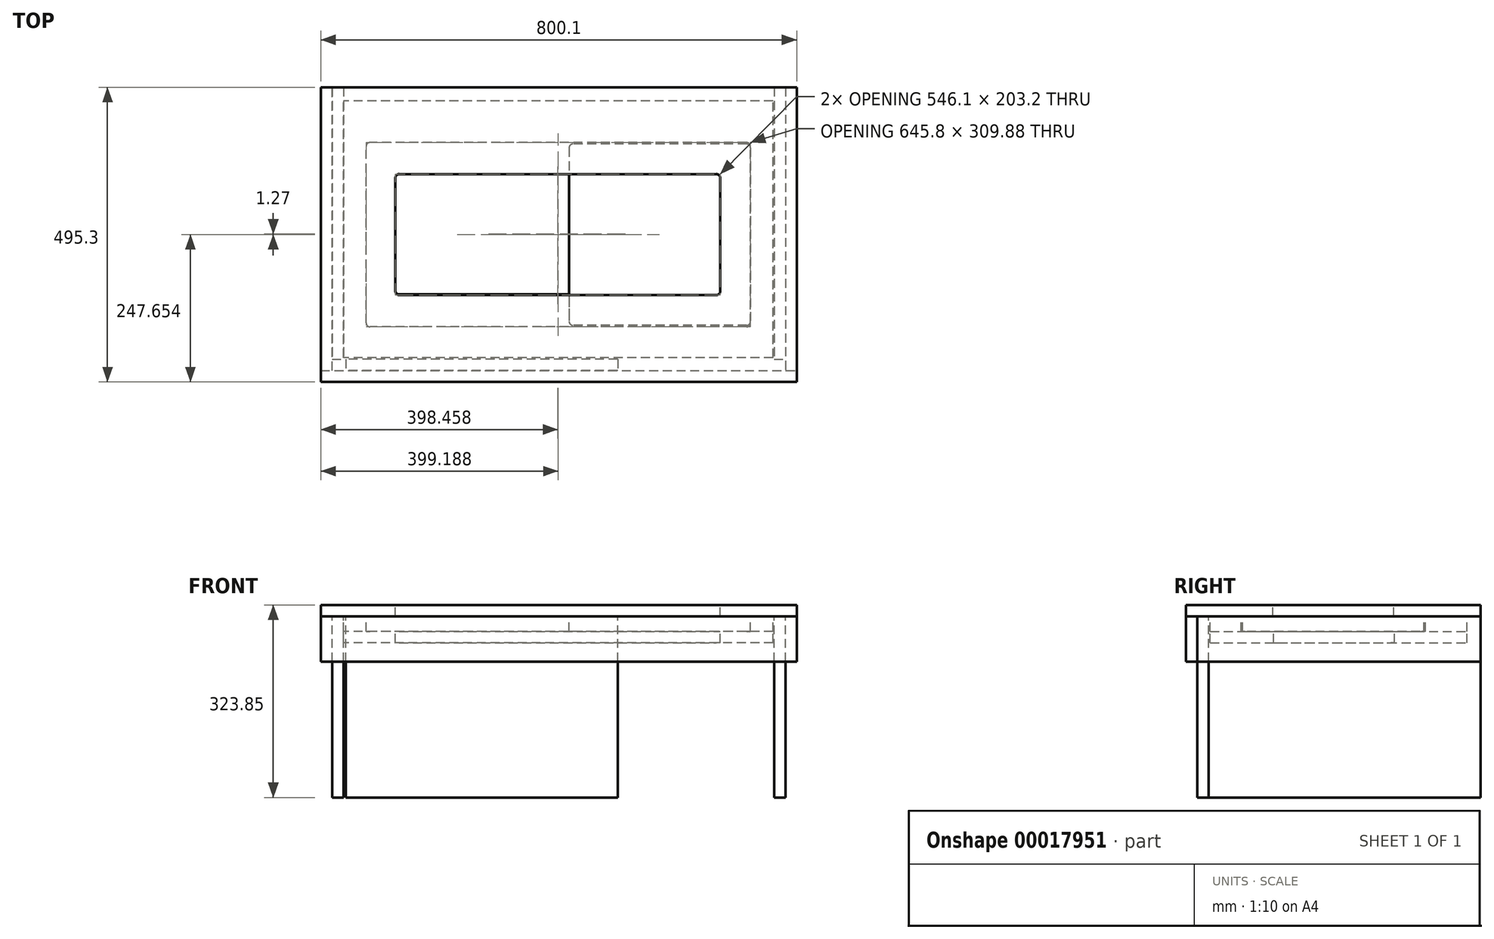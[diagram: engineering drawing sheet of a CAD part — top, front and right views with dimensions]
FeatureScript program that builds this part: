
annotation { "Feature Type Name" : "Feature", "Feature Type Description" : "" }
export const myFeature = defineFeature(function(context is Context, id is Id, definition is map)
    precondition{}
    {
        {
            var Q0;
            Q0=qCreatedBy(makeId("Top.planeOp"),FACE);
            var sketch = newSketch(context, id + "F0", { "sketchPlane" : qUnion([Q0])});
            skLineSegment(sketch, "E0.bottom", {"start": v(-395.07, 146.58) * mm, "end": v(405.03, 146.58) * mm});
            skLineSegment(sketch, "E0.top", {"start": v(-395.07, -348.72) * mm, "end": v(405.03, -348.72) * mm});
            skLineSegment(sketch, "E0.left", {"start": v(-395.07, 146.58) * mm, "end": v(-395.07, -348.72) * mm});
            skLineSegment(sketch, "E0.right", {"start": v(405.03, 146.58) * mm, "end": v(405.03, -348.72) * mm});
            skSolve(sketch);
        }
        {
            var Q0;
            Q0 = qSketchRegion(id + "F0", true);
            extrude(context, id + "F1", {"entities" : qUnion([Q0]), "depth" : 19.05 * mm, "offsetDistance" : 25.4 * mm});
        }
        {
            var Q0;
            Q0=makeQuery(id+"F1.opExtrude","CAP_FACE",FACE,{"disambiguationData":[OSD([sQuery(id+"F0.wireOp",EDGE,"E0.bottom"),sQuery(id+"F0.wireOp",EDGE,"E0.top"),sQuery(id+"F0.wireOp",EDGE,"E0.left"),sQuery(id+"F0.wireOp",EDGE,"E0.right")])],"isStart":false});
            var sketch = newSketch(context, id + "F2", { "sketchPlane" : qUnion([Q0])});
            skLineSegment(sketch, "E1.bottom", {"start": v(-269.66, 0.53) * mm, "end": v(276.44, 0.53) * mm});
            skLineSegment(sketch, "E1.top", {"start": v(-269.66, -202.67) * mm, "end": v(276.44, -202.67) * mm});
            skLineSegment(sketch, "E1.left", {"start": v(-269.66, 0.53) * mm, "end": v(-269.66, -202.67) * mm});
            skLineSegment(sketch, "E1.right", {"start": v(276.44, 0.53) * mm, "end": v(276.44, -202.67) * mm});
            skSolve(sketch);
        }
        {
            var Q0;
            Q0 = qSketchRegion(id + "F2", true);
            extrude(context, id + "F3", {"entities" : qUnion([Q0]), "operationType" : NewBodyOperationType.REMOVE, "oppositeDirection" : true, "depth" : 25.4 * mm, "offsetDistance" : 25.4 * mm});
        }
        {
            var Q0;
            Q0=makeQuery(id+"F3.boolean.opBoolean","COPY",EDGE,{"derivedFrom":makeQuery(id+"F3.opExtrude","SWEPT_EDGE",EDGE,{"disambiguationData":[OSD([sQuery(id+"F2.wireOp",EDGE,"E1.bottom"),sQuery(id+"F2.wireOp",EDGE,"E1.left")])]})});
            var Q1;
            Q1=makeQuery(id+"F3.boolean.opBoolean","COPY",EDGE,{"derivedFrom":makeQuery(id+"F3.opExtrude","SWEPT_EDGE",EDGE,{"disambiguationData":[OSD([sQuery(id+"F2.wireOp",EDGE,"E1.bottom"),sQuery(id+"F2.wireOp",EDGE,"E1.right")])]})});
            var Q2;
            Q2=makeQuery(id+"F3.boolean.opBoolean","COPY",EDGE,{"derivedFrom":makeQuery(id+"F3.opExtrude","SWEPT_EDGE",EDGE,{"disambiguationData":[OSD([sQuery(id+"F2.wireOp",EDGE,"E1.top"),sQuery(id+"F2.wireOp",EDGE,"E1.right")])]})});
            var Q3;
            Q3=makeQuery(id+"F3.boolean.opBoolean","COPY",EDGE,{"derivedFrom":makeQuery(id+"F3.opExtrude","SWEPT_EDGE",EDGE,{"disambiguationData":[OSD([sQuery(id+"F2.wireOp",EDGE,"E1.top"),sQuery(id+"F2.wireOp",EDGE,"E1.left")])]})});
            fillet(context, id + "F4", {"entities" : qUnion([Q0, Q1, Q2, Q3]), "radius" : 6.35 * mm, "tangentPropagation" : true, "allowEdgeOverflow" : false});
        }
        {
            var Q0;
            Q0=makeQuery(id+"F1.opExtrude","CAP_FACE",FACE,{"disambiguationData":[OSD([sQuery(id+"F0.wireOp",EDGE,"E0.bottom"),sQuery(id+"F0.wireOp",EDGE,"E0.top"),sQuery(id+"F0.wireOp",EDGE,"E0.left"),sQuery(id+"F0.wireOp",EDGE,"E0.right")])],"isStart":true});
            var sketch = newSketch(context, id + "F5", { "sketchPlane" : qUnion([Q0])});
            skLineSegment(sketch, "E2.bottom", {"start": v(-395.07, 348.72) * mm, "end": v(405.03, 348.72) * mm});
            skLineSegment(sketch, "E2.top", {"start": v(-395.07, 329.67) * mm, "end": v(405.03, 329.67) * mm});
            skLineSegment(sketch, "E2.left", {"start": v(-395.07, 348.72) * mm, "end": v(-395.07, 329.67) * mm});
            skLineSegment(sketch, "E2.right", {"start": v(405.03, 348.72) * mm, "end": v(405.03, 329.67) * mm});
            skSolve(sketch);
        }
        {
            var Q0;
            Q0 = qSketchRegion(id + "F5", true);
            extrude(context, id + "F6", {"entities" : qUnion([Q0]), "depth" : 76.2 * mm, "offsetDistance" : 25.4 * mm});
        }
        {
            var Q0;
            Q0=makeQuery(id+"F1.opExtrude","CAP_FACE",FACE,{"disambiguationData":[OSD([sQuery(id+"F0.wireOp",EDGE,"E0.bottom"),sQuery(id+"F0.wireOp",EDGE,"E0.top"),sQuery(id+"F0.wireOp",EDGE,"E0.left"),sQuery(id+"F0.wireOp",EDGE,"E0.right")])],"isStart":true});
            var sketch = newSketch(context, id + "F7", { "sketchPlane" : qUnion([Q0])});
            skLineSegment(sketch, "E3.bottom", {"start": v(-395.07, 329.67) * mm, "end": v(-376.02, 329.67) * mm});
            skLineSegment(sketch, "E3.top", {"start": v(-395.07, -146.58) * mm, "end": v(-376.02, -146.58) * mm});
            skLineSegment(sketch, "E3.left", {"start": v(-395.07, 329.67) * mm, "end": v(-395.07, -146.58) * mm});
            skLineSegment(sketch, "E3.right", {"start": v(-376.02, 329.67) * mm, "end": v(-376.02, -146.58) * mm});
            skSolve(sketch);
        }
        {
            var Q0;
            Q0 = qSketchRegion(id + "F7", true);
            extrude(context, id + "F8", {"entities" : qUnion([Q0]), "depth" : 76.2 * mm, "offsetDistance" : 25.4 * mm});
        }
        {
            var Q0;
            Q0=makeQuery(id+"F8.opExtrude","SWEPT_BODY",BODY,{"disambiguationData":[OSD([sQuery(id+"F7.wireOp",EDGE,"E3.bottom"),sQuery(id+"F7.wireOp",EDGE,"E3.top"),sQuery(id+"F7.wireOp",EDGE,"E3.left"),sQuery(id+"F7.wireOp",EDGE,"E3.right")])]});
            transform(context, id + "F9", {"entities" : qUnion([Q0]), "transformType" : TransformType.TRANSLATION_3D, "dx" : 781.05 * mm, "dy" : 0 * mm, "dz" : 0 * mm, "makeCopy" : true});
        }
        {
            var Q0;
            Q0=makeQuery(id+"F1.opExtrude","CAP_FACE",FACE,{"disambiguationData":[OSD([sQuery(id+"F0.wireOp",EDGE,"E0.bottom"),sQuery(id+"F0.wireOp",EDGE,"E0.top"),sQuery(id+"F0.wireOp",EDGE,"E0.left"),sQuery(id+"F0.wireOp",EDGE,"E0.right")])],"isStart":true});
            var sketch = newSketch(context, id + "F10", { "sketchPlane" : qUnion([Q0])});
            skLineSegment(sketch, "E4.bottom", {"start": v(327.24, -51.33) * mm, "end": v(22.44, -51.33) * mm});
            skLineSegment(sketch, "E4.top", {"start": v(327.24, 253.47) * mm, "end": v(22.44, 253.47) * mm});
            skLineSegment(sketch, "E4.left", {"start": v(327.24, -51.33) * mm, "end": v(327.24, 253.47) * mm});
            skLineSegment(sketch, "E4.right", {"start": v(22.44, -51.33) * mm, "end": v(22.44, 253.47) * mm});
            skSolve(sketch);
        }
        {
            var Q0;
            Q0 = qSketchRegion(id + "F10", true);
            extrude(context, id + "F11", {"entities" : qUnion([Q0]), "depth" : 25.4 * mm, "offsetDistance" : 25.4 * mm});
        }
        {
            var Q0;
            Q0=makeQuery(id+"F11.opExtrude","SWEPT_EDGE",EDGE,{"disambiguationData":[OSD([sQuery(id+"F10.wireOp",EDGE,"E4.bottom"),sQuery(id+"F10.wireOp",EDGE,"E4.left")])]});
            var Q1;
            Q1=makeQuery(id+"F11.opExtrude","SWEPT_EDGE",EDGE,{"disambiguationData":[OSD([sQuery(id+"F10.wireOp",EDGE,"E4.bottom"),sQuery(id+"F10.wireOp",EDGE,"E4.right")])]});
            var Q2;
            Q2=makeQuery(id+"F11.opExtrude","SWEPT_EDGE",EDGE,{"disambiguationData":[OSD([sQuery(id+"F10.wireOp",EDGE,"E4.top"),sQuery(id+"F10.wireOp",EDGE,"E4.left")])]});
            var Q3;
            Q3=makeQuery(id+"F11.opExtrude","SWEPT_EDGE",EDGE,{"disambiguationData":[OSD([sQuery(id+"F10.wireOp",EDGE,"E4.top"),sQuery(id+"F10.wireOp",EDGE,"E4.right")])]});
            fillet(context, id + "F12", {"entities" : qUnion([Q0, Q1, Q2, Q3]), "radius" : 6.35 * mm, "tangentPropagation" : true, "allowEdgeOverflow" : false});
        }
        {
            var Q0;
            Q0=makeQuery(id+"F1.opExtrude","CAP_FACE",FACE,{"disambiguationData":[OSD([sQuery(id+"F0.wireOp",EDGE,"E0.bottom"),sQuery(id+"F0.wireOp",EDGE,"E0.top"),sQuery(id+"F0.wireOp",EDGE,"E0.left"),sQuery(id+"F0.wireOp",EDGE,"E0.right")])],"isStart":true});
            var sketch = newSketch(context, id + "F13", { "sketchPlane" : qUnion([Q0])});
            skLineSegment(sketch, "E5.bottom", {"start": v(-376.02, -146.58) * mm, "end": v(-356.97, -146.58) * mm});
            skLineSegment(sketch, "E5.top", {"start": v(-376.02, 310.62) * mm, "end": v(-356.97, 310.62) * mm});
            skLineSegment(sketch, "E5.left", {"start": v(-376.02, -146.58) * mm, "end": v(-376.02, 310.62) * mm});
            skLineSegment(sketch, "E5.right", {"start": v(-356.97, -146.58) * mm, "end": v(-356.97, 310.62) * mm});
            skSolve(sketch);
        }
        {
            var Q0;
            Q0 = qSketchRegion(id + "F13", true);
            extrude(context, id + "F14", {"entities" : qUnion([Q0]), "depth" : 304.8 * mm, "offsetDistance" : 25.4 * mm});
        }
        {
            var Q0;
            Q0=makeQuery(id+"F14.opExtrude","SWEPT_BODY",BODY,{"disambiguationData":[OSD([sQuery(id+"F13.wireOp",EDGE,"E5.bottom"),sQuery(id+"F13.wireOp",EDGE,"E5.top"),sQuery(id+"F13.wireOp",EDGE,"E5.left"),sQuery(id+"F13.wireOp",EDGE,"E5.right")])]});
            transform(context, id + "F15", {"entities" : qUnion([Q0]), "transformType" : TransformType.TRANSLATION_3D, "dx" : 742.95 * mm, "dy" : 0 * mm, "dz" : 0 * mm, "makeCopy" : true});
        }
        {
            var Q0;
            Q0=makeQuery(id+"F14.opExtrude","SWEPT_BODY",BODY,{"disambiguationData":[OSD([sQuery(id+"F13.wireOp",EDGE,"E5.bottom"),sQuery(id+"F13.wireOp",EDGE,"E5.top"),sQuery(id+"F13.wireOp",EDGE,"E5.left"),sQuery(id+"F13.wireOp",EDGE,"E5.right")])]});
            var Q1;
            Q1=makeQuery(id+"F14.opExtrude","SWEPT_EDGE",EDGE,{"disambiguationData":[OSD([sQuery(id+"F13.wireOp",EDGE,"E5.top"),sQuery(id+"F13.wireOp",EDGE,"E5.right")])]});
            transform(context, id + "F16", {"entities" : qUnion([Q0]), "transformType" : TransformType.ROTATION, "transformAxis" : qUnion([Q1]), "angle" : 90 * degree, "oppositeDirection" : true, "makeCopy" : true});
        }
        {
            var Q0;
            Q0=makeQuery(id+"F16.opPattern","COPY",BODY,{"derivedFrom":makeQuery(id+"F14.opExtrude","SWEPT_BODY",BODY,{"disambiguationData":[OSD([sQuery(id+"F13.wireOp",EDGE,"E5.bottom"),sQuery(id+"F13.wireOp",EDGE,"E5.top"),sQuery(id+"F13.wireOp",EDGE,"E5.left"),sQuery(id+"F13.wireOp",EDGE,"E5.right")])]}),"instanceName":"1"});
            transform(context, id + "F17", {"entities" : qUnion([Q0]), "transformType" : TransformType.TRANSLATION_3D, "dx" : (((31.5) / 2) - 12) * mm, "dy" : -19.05 * mm, "dz" : 0 * mm, "makeCopy" : false});
        }
        {
            var Q0;
            Q0=makeQuery(id+"F1.opExtrude","CAP_FACE",FACE,{"disambiguationData":[OSD([sQuery(id+"F0.wireOp",EDGE,"E0.bottom"),sQuery(id+"F0.wireOp",EDGE,"E0.top"),sQuery(id+"F0.wireOp",EDGE,"E0.left"),sQuery(id+"F0.wireOp",EDGE,"E0.right")])],"isStart":true});
            var sketch = newSketch(context, id + "F18", { "sketchPlane" : qUnion([Q0])});
            skLineSegment(sketch, "E6.bottom", {"start": v(365.12, 308.08) * mm, "end": v(-356.88, 308.08) * mm});
            skLineSegment(sketch, "E6.top", {"start": v(365.12, -123.72) * mm, "end": v(-356.88, -123.72) * mm});
            skLineSegment(sketch, "E6.left", {"start": v(365.12, 308.08) * mm, "end": v(365.12, -123.72) * mm});
            skLineSegment(sketch, "E6.right", {"start": v(-356.88, 308.08) * mm, "end": v(-356.88, -123.72) * mm});
            skLineSegment(sketch, "E7.bottom", {"start": v(327.02, 256) * mm, "end": v(-318.78, 256) * mm});
            skLineSegment(sketch, "E7.top", {"start": v(327.02, -53.87) * mm, "end": v(-318.78, -53.87) * mm});
            skLineSegment(sketch, "E7.left", {"start": v(327.02, 256) * mm, "end": v(327.02, -53.87) * mm});
            skLineSegment(sketch, "E7.right", {"start": v(-318.78, 256) * mm, "end": v(-318.78, -53.87) * mm});
            skSolve(sketch);
        }
        {
            var Q0;
            Q0=makeQuery(id+"F18.imprint","IMPRINT",FACE,{"disambiguationData":[TD([[makeQuery(id+"F18.imprint","IMPRINT",EDGE,{"derivedFrom":sQuery(id+"F18.wireOp",EDGE,"E6.bottom")}),1.0]])]});
            extrude(context, id + "F19", {"entities" : qUnion([Q0]), "depth" : 25.4 * mm, "offsetDistance" : 25.4 * mm});
        }
        {
            var Q0;
            Q0=makeQuery(id+"F19.opExtrude","SWEPT_EDGE",EDGE,{"disambiguationData":[OSD([sQuery(id+"F18.wireOp",EDGE,"E7.bottom"),sQuery(id+"F18.wireOp",EDGE,"E7.right")])]});
            var Q1;
            Q1=makeQuery(id+"F19.opExtrude","SWEPT_EDGE",EDGE,{"disambiguationData":[OSD([sQuery(id+"F18.wireOp",EDGE,"E7.top"),sQuery(id+"F18.wireOp",EDGE,"E7.right")])]});
            var Q2;
            Q2=makeQuery(id+"F19.opExtrude","SWEPT_EDGE",EDGE,{"disambiguationData":[OSD([sQuery(id+"F18.wireOp",EDGE,"E7.top"),sQuery(id+"F18.wireOp",EDGE,"E7.left")])]});
            var Q3;
            Q3=makeQuery(id+"F19.opExtrude","SWEPT_EDGE",EDGE,{"disambiguationData":[OSD([sQuery(id+"F18.wireOp",EDGE,"E7.bottom"),sQuery(id+"F18.wireOp",EDGE,"E7.left")])]});
            fillet(context, id + "F20", {"entities" : qUnion([Q0, Q1, Q2, Q3]), "radius" : 6.35 * mm, "tangentPropagation" : true, "allowEdgeOverflow" : false});
        }
        {
            var Q0;
            Q0=makeQuery(id+"F19.opExtrude","CAP_FACE",FACE,{"disambiguationData":[OSD([sQuery(id+"F18.wireOp",EDGE,"E6.bottom"),sQuery(id+"F18.wireOp",EDGE,"E6.top"),sQuery(id+"F18.wireOp",EDGE,"E6.left"),sQuery(id+"F18.wireOp",EDGE,"E6.right"),sQuery(id+"F18.wireOp",EDGE,"E7.bottom"),sQuery(id+"F18.wireOp",EDGE,"E7.top"),sQuery(id+"F18.wireOp",EDGE,"E7.left"),sQuery(id+"F18.wireOp",EDGE,"E7.right")])],"isStart":false});
            var sketch = newSketch(context, id + "F21", { "sketchPlane" : qUnion([Q0])});
            skLineSegment(sketch, "E8.bottom", {"start": v(-356.88, 308.08) * mm, "end": v(365.12, 308.08) * mm});
            skLineSegment(sketch, "E8.top", {"start": v(-356.88, -123.72) * mm, "end": v(365.12, -123.72) * mm});
            skLineSegment(sketch, "E8.left", {"start": v(-356.88, 308.08) * mm, "end": v(-356.88, -123.72) * mm});
            skLineSegment(sketch, "E8.right", {"start": v(365.12, 308.08) * mm, "end": v(365.12, -123.72) * mm});
            skLineSegment(sketch, "E9.bottom", {"start": v(-269.66, 201.4) * mm, "end": v(276.44, 201.4) * mm});
            skLineSegment(sketch, "E9.top", {"start": v(-269.66, -1.8) * mm, "end": v(276.44, -1.8) * mm});
            skLineSegment(sketch, "E9.left", {"start": v(-269.66, 201.4) * mm, "end": v(-269.66, -1.8) * mm});
            skLineSegment(sketch, "E9.right", {"start": v(276.44, 201.4) * mm, "end": v(276.44, -1.8) * mm});
            skSolve(sketch);
        }
        {
            var Q0;
            Q0 = qSketchRegion(id + "F21", true);
            extrude(context, id + "F22", {"entities" : qUnion([Q0]), "depth" : 19.05 * mm, "offsetDistance" : 25.4 * mm});
        }
        {
            var Q0;
            Q0=makeQuery(id+"F22.opExtrude","SWEPT_EDGE",EDGE,{"disambiguationData":[OSD([sQuery(id+"F21.wireOp",EDGE,"E9.bottom"),sQuery(id+"F21.wireOp",EDGE,"E9.left")])]});
            var Q1;
            Q1=makeQuery(id+"F22.opExtrude","SWEPT_EDGE",EDGE,{"disambiguationData":[OSD([sQuery(id+"F21.wireOp",EDGE,"E9.top"),sQuery(id+"F21.wireOp",EDGE,"E9.left")])]});
            var Q2;
            Q2=makeQuery(id+"F22.opExtrude","SWEPT_EDGE",EDGE,{"disambiguationData":[OSD([sQuery(id+"F21.wireOp",EDGE,"E9.top"),sQuery(id+"F21.wireOp",EDGE,"E9.right")])]});
            var Q3;
            Q3=makeQuery(id+"F22.opExtrude","SWEPT_EDGE",EDGE,{"disambiguationData":[OSD([sQuery(id+"F21.wireOp",EDGE,"E9.bottom"),sQuery(id+"F21.wireOp",EDGE,"E9.right")])]});
            fillet(context, id + "F23", {"entities" : qUnion([Q0, Q1, Q2, Q3]), "radius" : 6.35 * mm, "tangentPropagation" : true, "allowEdgeOverflow" : false});
        }
    });
